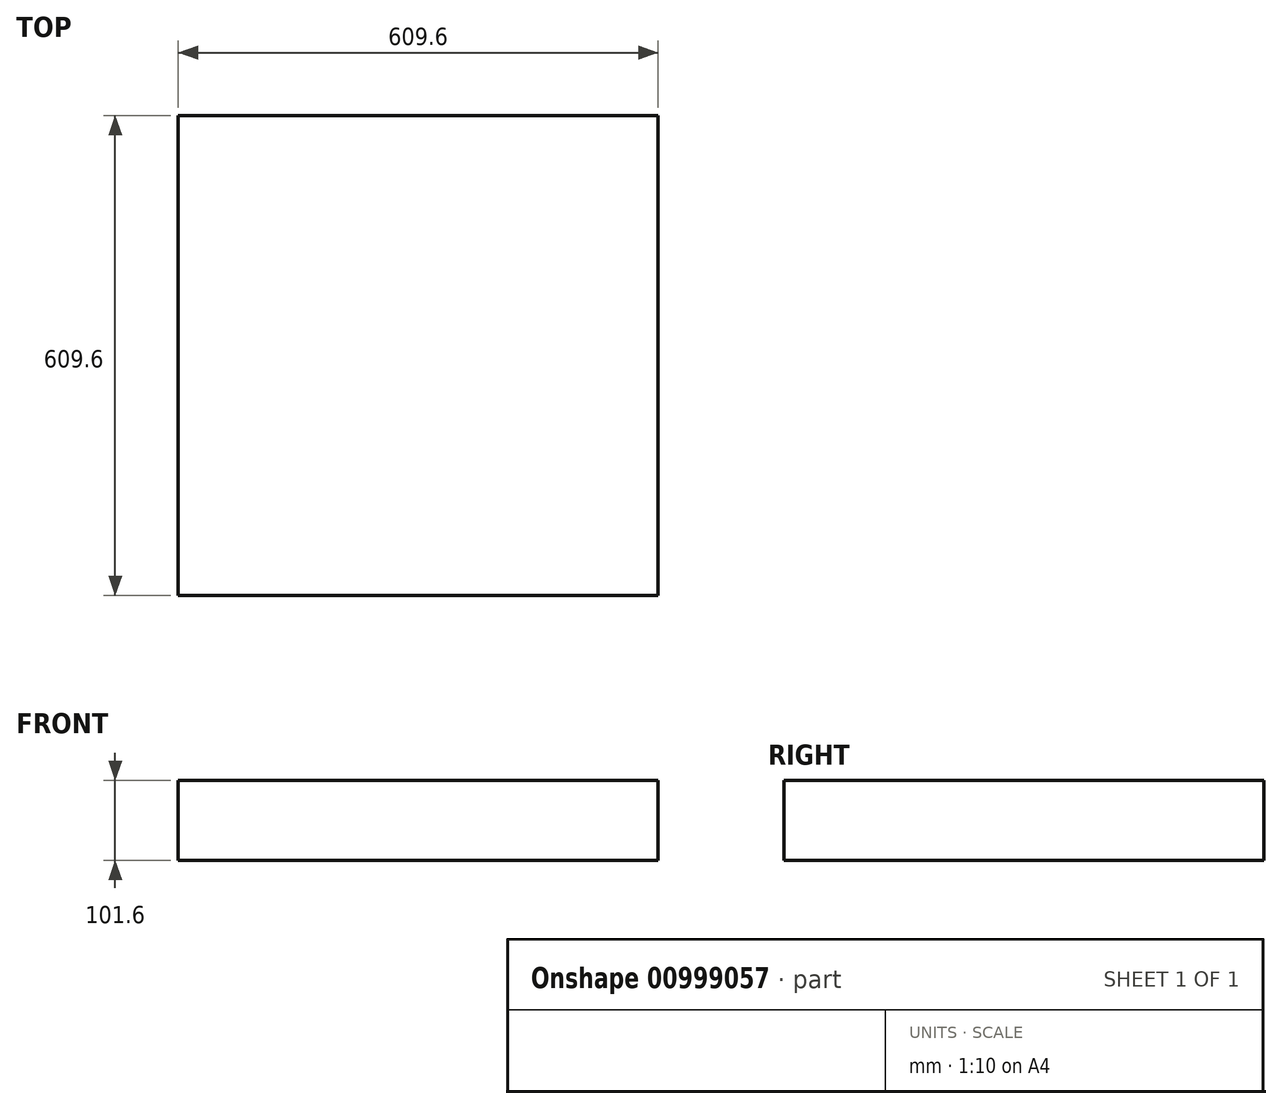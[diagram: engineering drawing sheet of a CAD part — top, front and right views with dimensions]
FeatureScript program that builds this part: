
annotation { "Feature Type Name" : "Feature", "Feature Type Description" : "" }
export const myFeature = defineFeature(function(context is Context, id is Id, definition is map)
    precondition{}
    {
        {
            var Q0;
            Q0=qCreatedBy(makeId("Front.planeOp"),FACE);
            var sketch = newSketch(context, id + "F0", { "sketchPlane" : qUnion([Q0])});
            skLineSegment(sketch, "E0.bottom", {"start": v(0, 0) * mm, "end": v(609.6, 0) * mm});
            skLineSegment(sketch, "E0.top", {"start": v(0, 101.6) * mm, "end": v(609.6, 101.6) * mm});
            skLineSegment(sketch, "E0.left", {"start": v(0, 0) * mm, "end": v(0, 101.6) * mm});
            skLineSegment(sketch, "E0.right", {"start": v(609.6, 0) * mm, "end": v(609.6, 101.6) * mm});
            skSolve(sketch);
        }
        {
            var Q0;
            Q0 = qSketchRegion(id + "F0", true);
            extrude(context, id + "F1", {"entities" : qUnion([Q0]), "depth" : 609.6 * mm, "offsetDistance" : 25.4 * mm});
        }
    });
